# Revit family: Faucet-Lavatory-KOHLER-PURIST-K-7505T
name_source: partatom
category: Plumbing Fixtures
revit_build: Autodesk Revit 2017 (Build: 20160225_1515(x64)
units: mm (PartAtom-declared; Revit-internal decimal feet)

## family parameters
Cut with Voids When Loaded = No
Host = Face
OmniClass Number = 23.31.11.00
OmniClass Title = Faucets
Part Type = Normal
Room Calculation Point = No
Round Connector Dimension = Use Diameter
Shared = No

## types (6) — shared parameters
ADA Compliant = No
Assembly Code = D2010
CW Connection = Yes
Cold Water Inlet = Cold Water Inlet
Date Modified = 06/08/2020
Default Elevation = 36"
Drain Included = No
HW Connection = Yes
Handle Clearance = 3"
Height = 11 7/16"
Hot Water Inlet = Hot Water Inlet
Length = 8"
Manufacturer = KOHLER Co.
Master Format 2014 = 22 41 39
Master Format 2014 Name = Residential Faucets, Supplies, and Trim
Material = Premium Metal Construction
Pressure = 45.00 psi
Product Name = PURIST
Spout Reach = 8"
URL = http://www.kohler.com.cn
Vent Connection = No
Waste Connection = No
Waste Water Outlet = Waste Water Outlet
WaterSense Certified = No
Width = 4 11/16"

## per-type parameters (varying)
| type | Description | Finish | Flow Rate | Model | Product Documentation Link | Product Page URL | Type |
| 2.75 GPM, CP-Polished Chrome | Primary Pull-out | Kohler-Metal-CP-Polished_Chrome | 3 GPM | K-7505T-B4-CP |  |  | 1 |
| 2.275 GPM, BV-Roman Copper | Primary Pull-out | Kohler-Metal-BV-Roman_Copper | 3 GPM | K-7505T-B4-BV |  |  | 2 |
| 2.75 GPM, VS-Stainless Steel Wire Drawing | Primary Pull-out | Kohler-Metal-VS-Stainless_Steel_Wire_Drawing | 3 GPM | K-7505T-B4-BV |  |  | 2 |
| 2.2 GPM, CP-Polished Chrome | Pull-out Kitchen Faucet | Kohler-Metal-CP-Polished_Chrome | 2 GPM | K-7505T-C4-CP | https://files.kohler.com.cn | http://www.kohler.com.cn | 4 |
| 2.2 GPM, BV-Roman Copper | Pull-out Kitchen Faucet | Kohler-Metal-BV-Roman_Copper | 2 GPM | K-7505T-C4-BV | https://files.kohler.com.cn | http://www.kohler.com.cn | 5 |
| 2.2 GPM, VS-Stainless Steel Wire Drawing | Pull-out Kitchen Faucet | Kohler-Metal-VS-Stainless_Steel_Wire_Drawing | 2 GPM | K-7505T-C4-VS | https://files.kohler.com.cn | http://www.kohler.com.cn | 6 |

## geometry (parser evidence)
native form markers: Sweep x6
no freeform markers — native parametric forms only
